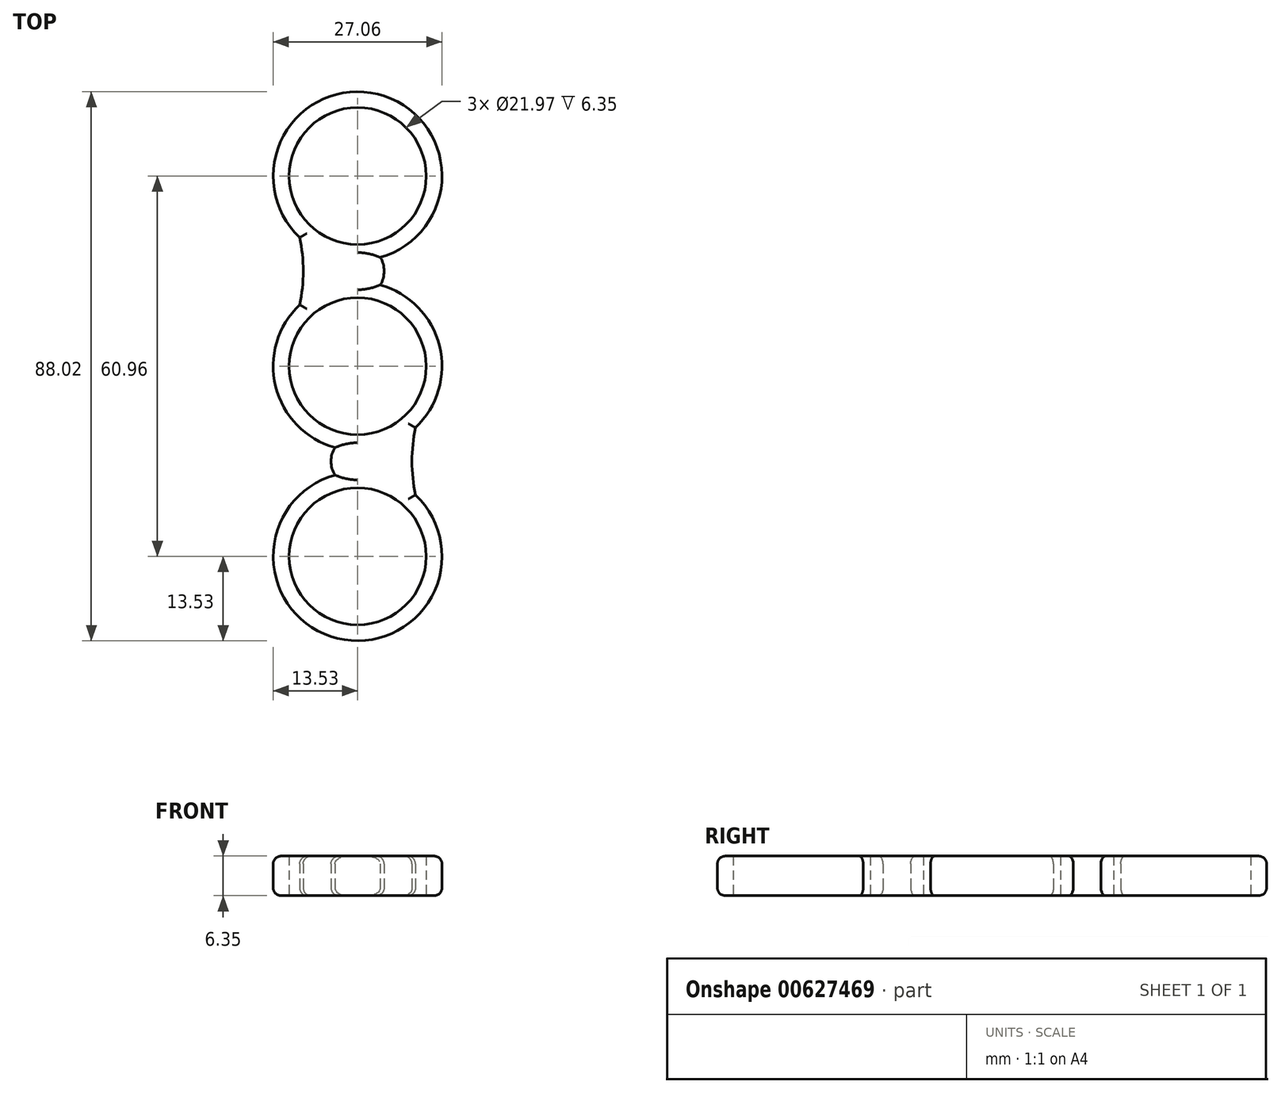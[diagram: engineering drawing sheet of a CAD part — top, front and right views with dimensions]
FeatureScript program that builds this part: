
annotation { "Feature Type Name" : "Feature", "Feature Type Description" : "" }
export const myFeature = defineFeature(function(context is Context, id is Id, definition is map)
    precondition{}
    {
        {
            var Q0;
            Q0=qCreatedBy(makeId("Top.planeOp"),FACE);
            var sketch = newSketch(context, id + "F0", { "sketchPlane" : qUnion([Q0])});
            skCircle(sketch, "E0", {"center": v(0, 0) * mm, "radius": 13.53 * mm});
            skLineSegment(sketch, "E1", {"start": v(0, 0) * mm, "end": v(0, 30.48) * mm});
            skLineSegment(sketch, "E2", {"start": v(0, 0) * mm, "end": v(0, -30.48) * mm});
            skCircle(sketch, "E3", {"center": v(0, -30.48) * mm, "radius": 13.53 * mm});
            skCircle(sketch, "E4", {"center": v(0, 0) * mm, "radius": 10.99 * mm});
            skCircle(sketch, "E5", {"center": v(0, 30.48) * mm, "radius": 10.99 * mm});
            skCircle(sketch, "E6", {"center": v(0, -30.48) * mm, "radius": 10.99 * mm});
            skCircle(sketch, "E7", {"center": v(0, 30.48) * mm, "radius": 13.53 * mm});
            skCircle(sketch, "E8", {"center": v(0, 15.24) * mm, "radius": 4.25 * mm});
            skCircle(sketch, "E9", {"center": v(0, -15.24) * mm, "radius": 4.25 * mm});
            skArc(sketch, "E10", {"start": v(9.27, -9.85) * mm, "mid": v(8.72, -15.24) * mm, "end": v(9.27, -20.63) * mm});
            skArc(sketch, "E11", {"start": v(-9.27, 9.85) * mm, "mid": v(-8.72, 15.24) * mm, "end": v(-9.27, 20.63) * mm});
            skPoint(sketch, "E12.orphan", {"position": v(-13.53, 30.48) * mm});
            skPoint(sketch, "E13.orphan", {"position": v(-13.53, 0) * mm});
            skPoint(sketch, "E14.orphan", {"position": v(13.53, 0) * mm});
            skPoint(sketch, "E15.orphan", {"position": v(13.53, -30.48) * mm});
            skSolve(sketch);
        }
        {
            var Q0;
            Q0 = qSketchRegion(id + "F0", true);
            var Q1;
            {var subQ0=sQuery(id+"F0.wireOp",EDGE,"E2");var subQ1=sQuery(id+"F0.wireOp",EDGE,"E0");var subQ2=makeQuery(id+"F0.imprint","INTERSECT",VERTEX,{"derivedFrom":[subQ1,subQ0]});Q1=makeQuery(id+"F0.imprint","IMPRINT",FACE,{"disambiguationData":[TD([[makeQuery(id+"F0.imprint","IMPRINT",EDGE,{"disambiguationData":[TD([[subQ2,-1.0]])],"derivedFrom":subQ1}),-1.0]])]});}
            var Q2;
            {var subQ0=sQuery(id+"F0.wireOp",EDGE,"E2");var subQ1=sQuery(id+"F0.wireOp",EDGE,"E0");var subQ2=makeQuery(id+"F0.imprint","INTERSECT",VERTEX,{"derivedFrom":[subQ1,subQ0]});Q2=makeQuery(id+"F0.imprint","IMPRINT",FACE,{"disambiguationData":[TD([[makeQuery(id+"F0.imprint","IMPRINT",EDGE,{"disambiguationData":[TD([[subQ2,-1.0]])],"derivedFrom":subQ1}),1.0]])]});}
            var Q3;
            {var subQ0=sQuery(id+"F0.wireOp",EDGE,"E3");var subQ1=sQuery(id+"F0.wireOp",EDGE,"E2");var subQ2=makeQuery(id+"F0.imprint","INTERSECT",VERTEX,{"derivedFrom":[subQ1,subQ0]});Q3=makeQuery(id+"F0.imprint","IMPRINT",FACE,{"disambiguationData":[TD([[makeQuery(id+"F0.imprint","IMPRINT",EDGE,{"disambiguationData":[TD([[subQ2,1.0]])],"derivedFrom":subQ0}),1.0]])]});}
            var Q4;
            {var subQ0=sQuery(id+"F0.wireOp",EDGE,"E1");var subQ1=sQuery(id+"F0.wireOp",EDGE,"E0");var subQ2=makeQuery(id+"F0.imprint","INTERSECT",VERTEX,{"derivedFrom":[subQ1,subQ0]});Q4=makeQuery(id+"F0.imprint","IMPRINT",FACE,{"disambiguationData":[TD([[makeQuery(id+"F0.imprint","IMPRINT",EDGE,{"disambiguationData":[TD([[subQ2,-1.0]])],"derivedFrom":subQ1}),-1.0]])]});}
            var Q5;
            {var subQ0=sQuery(id+"F0.wireOp",EDGE,"E7");var subQ1=sQuery(id+"F0.wireOp",EDGE,"E1");var subQ2=makeQuery(id+"F0.imprint","INTERSECT",VERTEX,{"derivedFrom":[subQ1,subQ0]});Q5=makeQuery(id+"F0.imprint","IMPRINT",FACE,{"disambiguationData":[TD([[makeQuery(id+"F0.imprint","IMPRINT",EDGE,{"disambiguationData":[TD([[subQ2,1.0]])],"derivedFrom":subQ0}),1.0]])]});}
            var Q6;
            {var subQ0=sQuery(id+"F0.wireOp",EDGE,"E1");var subQ1=sQuery(id+"F0.wireOp",EDGE,"E0");var subQ2=makeQuery(id+"F0.imprint","INTERSECT",VERTEX,{"derivedFrom":[subQ1,subQ0]});Q6=makeQuery(id+"F0.imprint","IMPRINT",FACE,{"disambiguationData":[TD([[makeQuery(id+"F0.imprint","IMPRINT",EDGE,{"disambiguationData":[TD([[subQ2,-1.0]])],"derivedFrom":subQ1}),1.0]])]});}
            extrude(context, id + "F1", {"entities" : qUnion([Q0, Q1, Q2, Q3, Q4, Q5, Q6]), "depth" : 6.35 * mm, "offsetDistance" : 25.4 * mm});
        }
        {
            var Q0;
            Q0=makeQuery(id+"F1.opExtrude","CAP_EDGE",EDGE,{"disambiguationData":[OSD([sQuery(id+"F0.wireOp",EDGE,"E7")])],"isStart":true});
            var Q1;
            Q1=makeQuery(id+"F1.opExtrude","CAP_EDGE",EDGE,{"disambiguationData":[OSD([sQuery(id+"F0.wireOp",EDGE,"E8")])],"isStart":true});
            var Q2;
            {var subQ0=sQuery(id+"F0.wireOp",EDGE,"E0");Q2=makeQuery(id+"F1.opExtrude","CAP_EDGE",EDGE,{"disambiguationData":[OSD([subQ0]),TDD([makeQuery(id+"F0.imprint","IMPRINT",EDGE,{"disambiguationData":[TD([[makeQuery(id+"F0.imprint","INTERSECT",VERTEX,{"derivedFrom":[subQ0,sQuery(id+"F0.wireOp",EDGE,"E10")]}),-1.0]])],"derivedFrom":subQ0})])],"isStart":true});}
            var Q3;
            Q3=makeQuery(id+"F1.opExtrude","CAP_EDGE",EDGE,{"disambiguationData":[OSD([sQuery(id+"F0.wireOp",EDGE,"E10")])],"isStart":true});
            var Q4;
            Q4=makeQuery(id+"F1.opExtrude","CAP_EDGE",EDGE,{"disambiguationData":[OSD([sQuery(id+"F0.wireOp",EDGE,"E3")])],"isStart":true});
            var Q5;
            Q5=makeQuery(id+"F1.opExtrude","CAP_EDGE",EDGE,{"disambiguationData":[OSD([sQuery(id+"F0.wireOp",EDGE,"E9")])],"isStart":true});
            var Q6;
            {var subQ0=sQuery(id+"F0.wireOp",EDGE,"E0");Q6=makeQuery(id+"F1.opExtrude","CAP_EDGE",EDGE,{"disambiguationData":[OSD([subQ0]),TDD([makeQuery(id+"F0.imprint","IMPRINT",EDGE,{"disambiguationData":[TD([[makeQuery(id+"F0.imprint","INTERSECT",VERTEX,{"derivedFrom":[subQ0,sQuery(id+"F0.wireOp",EDGE,"E11")]}),-1.0]])],"derivedFrom":subQ0})])],"isStart":true});}
            var Q7;
            Q7=makeQuery(id+"F1.opExtrude","CAP_EDGE",EDGE,{"disambiguationData":[OSD([sQuery(id+"F0.wireOp",EDGE,"E11")])],"isStart":true});
            var Q8;
            Q8=makeQuery(id+"F1.opExtrude","CAP_EDGE",EDGE,{"disambiguationData":[OSD([sQuery(id+"F0.wireOp",EDGE,"E7")])],"isStart":false});
            var Q9;
            Q9=makeQuery(id+"F1.opExtrude","CAP_EDGE",EDGE,{"disambiguationData":[OSD([sQuery(id+"F0.wireOp",EDGE,"E11")])],"isStart":false});
            var Q10;
            Q10=makeQuery(id+"F1.opExtrude","CAP_EDGE",EDGE,{"disambiguationData":[OSD([sQuery(id+"F0.wireOp",EDGE,"E8")])],"isStart":false});
            var Q11;
            {var subQ0=sQuery(id+"F0.wireOp",EDGE,"E0");Q11=makeQuery(id+"F1.opExtrude","CAP_EDGE",EDGE,{"disambiguationData":[OSD([subQ0]),TDD([makeQuery(id+"F0.imprint","IMPRINT",EDGE,{"disambiguationData":[TD([[makeQuery(id+"F0.imprint","INTERSECT",VERTEX,{"derivedFrom":[subQ0,sQuery(id+"F0.wireOp",EDGE,"E10")]}),-1.0]])],"derivedFrom":subQ0})])],"isStart":false});}
            var Q12;
            Q12=makeQuery(id+"F1.opExtrude","CAP_EDGE",EDGE,{"disambiguationData":[OSD([sQuery(id+"F0.wireOp",EDGE,"E10")])],"isStart":false});
            var Q13;
            {var subQ0=sQuery(id+"F0.wireOp",EDGE,"E0");Q13=makeQuery(id+"F1.opExtrude","CAP_EDGE",EDGE,{"disambiguationData":[OSD([subQ0]),TDD([makeQuery(id+"F0.imprint","IMPRINT",EDGE,{"disambiguationData":[TD([[makeQuery(id+"F0.imprint","INTERSECT",VERTEX,{"derivedFrom":[subQ0,sQuery(id+"F0.wireOp",EDGE,"E11")]}),-1.0]])],"derivedFrom":subQ0})])],"isStart":false});}
            var Q14;
            Q14=makeQuery(id+"F1.opExtrude","CAP_EDGE",EDGE,{"disambiguationData":[OSD([sQuery(id+"F0.wireOp",EDGE,"E9")])],"isStart":false});
            var Q15;
            Q15=makeQuery(id+"F1.opExtrude","CAP_EDGE",EDGE,{"disambiguationData":[OSD([sQuery(id+"F0.wireOp",EDGE,"E3")])],"isStart":false});
            fillet(context, id + "F2", {"entities" : qUnion([Q0, Q1, Q2, Q3, Q4, Q5, Q6, Q7, Q8, Q9, Q10, Q11, Q12, Q13, Q14, Q15]), "radius" : 1.27 * mm, "tangentPropagation" : true, "allowEdgeOverflow" : false});
        }
    });
